# Revit family: Door_Access_Fire-Wall_Acudor_FB-5060
name_source: partatom
category: Generic Models
units: mm (PartAtom-declared; Revit-internal decimal feet)

## family parameters
Can host rebar = No
Cut with Voids When Loaded = No
Host = Face
Part Type = Normal
Room Calculation Point = No
Round Connector Dimension = Use Diameter
Shared = No

## types (1)
- Door_Access_Fire-Wall_Acudor_FB-5060
    Clear Opening Height = 1' - 9"
    Clear Opening Width = 1' - 9"
    Default Elevation = 0' - 0"
    Description = Acudor Product as Specified
    Door Height = 2' - 5 3/4"
    Door Width = 1' - 9 3/4"
    Expected Lifespan (Years) = 0
    Fire Performance = as Specified
    Green Building-LEED = http://www.arcat.com
    Maintenance Schedule (Months) = 0
    Manufacturer = Acudor Products Inc
    Manufacturer Fax = 973-575-5160
    Manufacturer Website = http://www.acudor.com
    Model = As Specified
    Opening Height = 2' - 6 3/4"
    Opening Width = 1' - 10 3/4"
    Overall Height = 2' - 8"
    Overall Width = 2' - 0"
    Product Data = http://www.arcat.com
    Revision = R1_2017-03
    Sales Information = http://www.acudor.com
    Standards Conformance = as Specified
    URL = http://www.acudor.com
    Unit Depth = 0' - 2 9/16"
    Unit Height = 2' - 6"
    Unit Weight = 0
    Unit Width = 1' - 10"
    Warranty Duration (Years) = 0

## geometry (parser evidence)
native form markers: Sweep x1
no freeform markers — native parametric forms only
